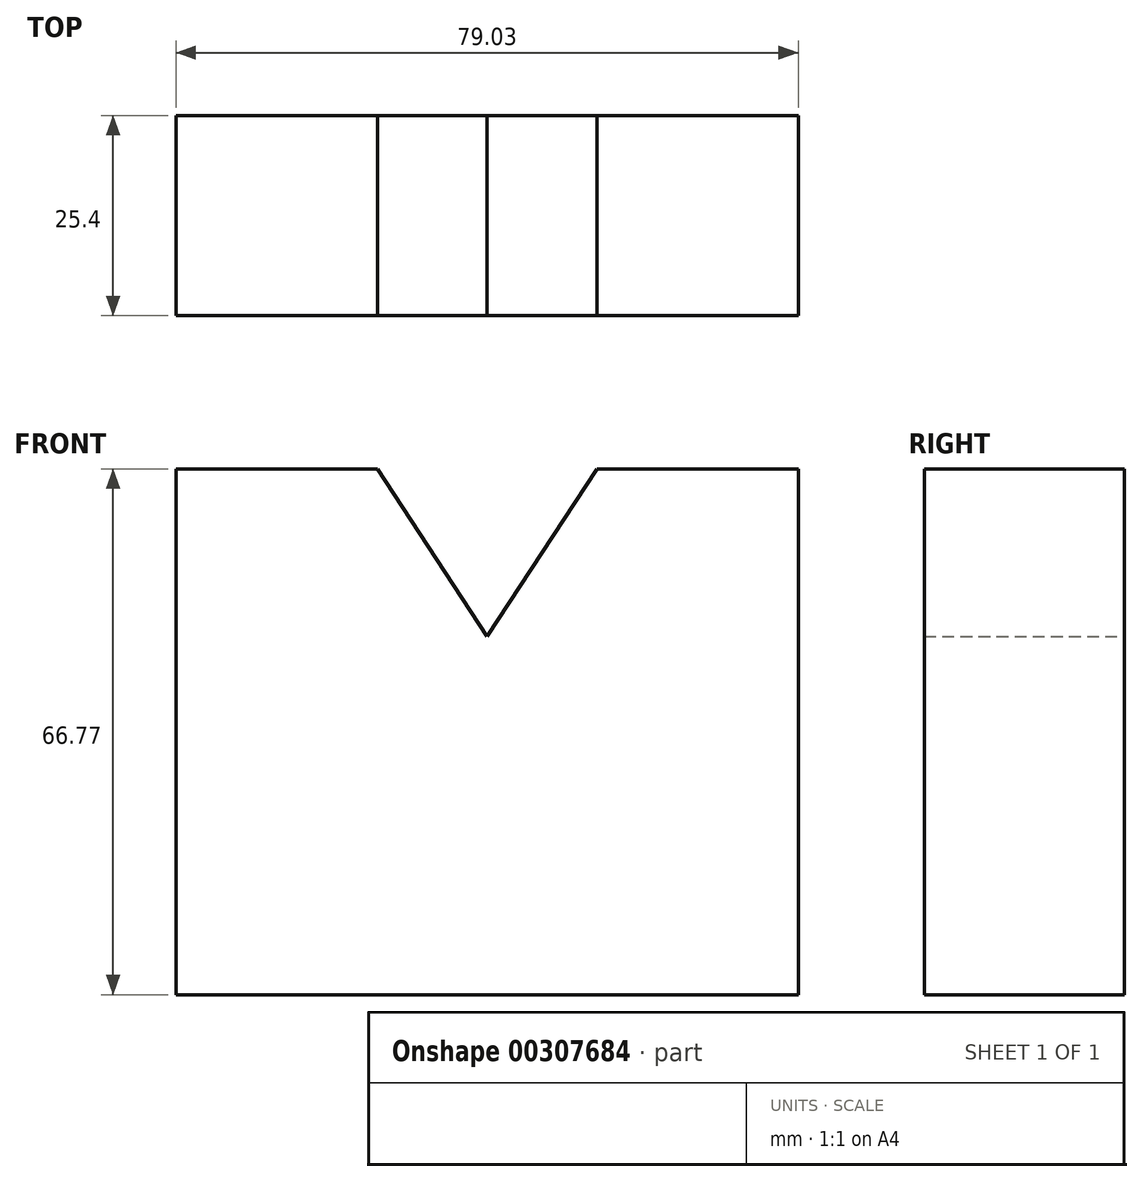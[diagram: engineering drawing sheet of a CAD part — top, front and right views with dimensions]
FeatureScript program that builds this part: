
annotation { "Feature Type Name" : "Feature", "Feature Type Description" : "" }
export const myFeature = defineFeature(function(context is Context, id is Id, definition is map)
    precondition{}
    {
        {
            var Q0;
            Q0=qCreatedBy(makeId("Front.planeOp"),FACE);
            var sketch = newSketch(context, id + "F0", { "sketchPlane" : qUnion([Q0])});
            skLineSegment(sketch, "E0", {"start": v(-44.56, -23.83) * mm, "end": v(34.47, -23.83) * mm});
            skLineSegment(sketch, "E1", {"start": v(34.47, -23.83) * mm, "end": v(34.47, 42.94) * mm});
            skLineSegment(sketch, "E2", {"start": v(34.47, 42.94) * mm, "end": v(-44.56, 42.94) * mm});
            skLineSegment(sketch, "E3", {"start": v(-44.56, 42.94) * mm, "end": v(-44.56, -23.83) * mm});
            skLineSegment(sketch, "E4", {"start": v(-18.98, 42.94) * mm, "end": v(-5.04, 21.7) * mm});
            skPoint(sketch, "E4.endSnap0", {"position": v(-5.04, 42.94) * mm});
            skLineSegment(sketch, "E5", {"start": v(-5.04, 21.7) * mm, "end": v(8.9, 42.94) * mm});
            skSolve(sketch);
        }
        {
            var Q0;
            Q0=makeQuery(id+"F0.imprint","IMPRINT",FACE,{"disambiguationData":[TD([[makeQuery(id+"F0.imprint","IMPRINT",EDGE,{"derivedFrom":sQuery(id+"F0.wireOp",EDGE,"E0")}),1.0]])]});
            extrude(context, id + "F1", {"entities" : qUnion([Q0]), "depth" : 25.4 * mm});
        }
    });
